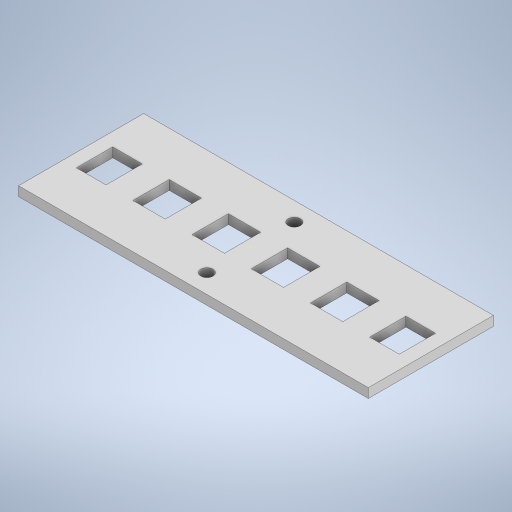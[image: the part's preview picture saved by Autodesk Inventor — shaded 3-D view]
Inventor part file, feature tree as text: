
AUTODESK INVENTOR PART (.ipt)
format: ipt  version: 2024 (Build 280153000, 153)  size: 283,136 bytes
history: native  units: mm
features: sketch x4, extrude x3
ambient origin geometry x8: Origin, YZ Plane, XZ Plane, XY Plane, X Axis, Y Axis, Z Axis, Center Point
bodies: Solid1 (feature_tree)
feature tree (7):
  extrude  "Extrusion1"  Depth=46.5mm
  extrude  "Extrusion3"  Depth=130.0mm
  sketch  "Sketch4"  dims[d5=3.5mm d6=0.0mm d21=16.5mm]
  extrude  "Extrusion4"  Depth=16.5mm
  sketch  "Sketch1"  dims[d1=46.5mm d2=23.25mm]
  sketch  "Sketch3"  dims[d3=130.0mm d4=67.0mm]
  sketch  "Sketch5"  dims[d22=16.5mm d23=5.0mm d24=10.0mm d25=10.0mm d26=10.0mm d27=10.0mm d28=5.0mm d29=16.0mm d30=38.0mm d31=60.0mm d32=60.0mm d33=38.0mm d34=16.0mm d35=10.0mm d36=0.0mm d37=4.5mm d38=4.5mm d39=7.0mm d40=67.0mm d41=7.0mm d42=67.0mm d43=3.5mm d44=0.0mm d45=0.5mm d46=0.872665mm]
